# Revit family: HandDryer_SurfaceMount_ASIJDMacDonald_TurboSlim
name_source: partatom
category: Specialty Equipment
revit_build: Autodesk Revit 2016 (Build: 20190508_0715(x64)
units: mm (PartAtom-declared; Revit-internal decimal feet)

## family parameters
Always vertical = Yes
Cut with Voids When Loaded = Yes
OmniClass Number = 23.40.20.21.14
OmniClass Title = Hand and Hair Dryers
Part Type = Normal
Room Calculation Point = No
Round Connector Dimension = Use Diameter
Shared = No
Work Plane-Based = No

## types (3) — shared parameters
Manufacturer = ASI JD MacDonald
Manufacturer_Overall Depth = 102 mm
Manufacturer_Overall Height = 216 mm
Manufacturer_Overall Width = 270 mm
Manufacturer_URL__Product Specific = https://jdmacdonald.com.au
ModifiedIssue_ANZRS = 20190912 $
URL = www.asijdmacdonald.com.au
Voltage = 240 V
zero-valued in all types: Cost

## per-type parameters (varying)
| type | Body Material | Description | Manufacturer_Spec Code | Model | Type Comments |
| White (10-0199-2-00) | z_ASI JD MacDonald_Steel_White Powder Coated | Turbo-Slim™ High-Speed Hand Dryer – White (10-0199-2-00) | 10-0199-2-00 | 10-0199-2-00 | Hand Dryer - Surface Mount - Turbo Slim - White |
| Satin (10-0199-2-93) | z_ASI JD MacDonald_Stainless Steel | Turbo-Slim™ High-Speed Hand Dryer – Satin Stainless Steel (10-0199-2-93) | 10-0199-2-93 | 10-0199-2-93 | Hand Dryer - Surface Mount - Turbo Slim - Satin Stainless Steel |
| Matte Black (10-0199-2-41) | z_ASI JD MacDonald_Steel_Matte Black Powder Coated | Turbo-Slim™ High-Speed Hand Dryer – Matte Black (10-0199-2-41) | 10-0199-2-41 | 10-0199-2-41 | Hand Dryer - Surface Mount - Turbo Slim - Matte Black |

## geometry (parser evidence)
native form markers: Sweep x3
no freeform markers — native parametric forms only
